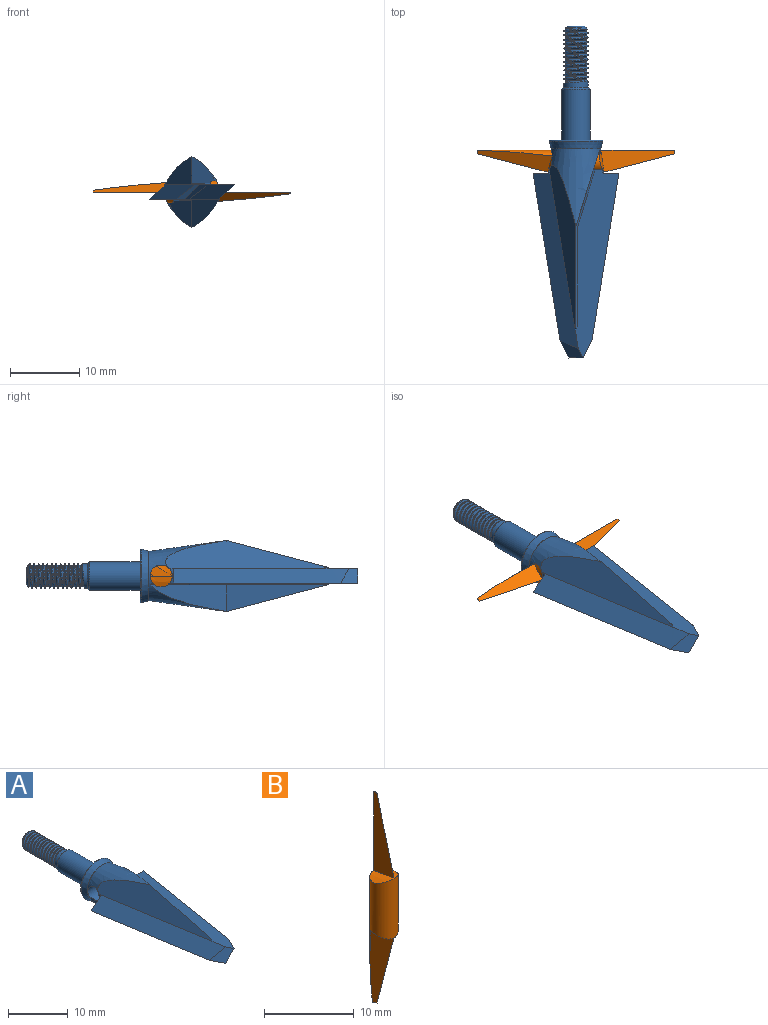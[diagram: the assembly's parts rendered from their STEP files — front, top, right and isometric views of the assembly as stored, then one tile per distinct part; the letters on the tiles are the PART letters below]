
ASSEMBLY  parts=2 mates=1
PART A: 56 faces, bbox 12.4x48x10.3 mm
  f0: plane 23.64x4.12mm, normal (0.85,-0.14,-0.52), area 71mm2, adj f1,f4,f5,f27,f29,f53,f55
  f1: plane 14.73x0.25mm, normal (-0.71,0,-0.71), area 5.2mm2, adj f0,f10,f29,f51,f55
  f2: plane 23.86x4.12mm, normal (-0.85,-0.14,0.52), area 71mm2, adj f3,f5,f9,f23,f28,f53,f54
  f3: plane 14.73x0.25mm, normal (0.71,0,0.71), area 5.2mm2, adj f2,f8,f12,f23,f54
  f4: plane 0.56x0.18mm, normal (0,0,-1), area 0.1mm2, adj f0,f7,f16,f53
  f5: cone r=3.56mm half-angle=8deg, axis (0,-1,0), area 89.4mm2, adj f0,f2,f11,f19,f23,f24,f29,f30
  f6: cone r=3.56mm half-angle=8deg, axis (0,-1,0), area 0.6mm2, adj f9,f10,f18,f31,f53
  f7: cone r=3.56mm half-angle=8deg, axis (0,-1,0), area 0.6mm2, adj f4,f8,f16,f17,f53
  f8: plane 27.23x6.33mm, normal (0,0,1), area 91.9mm2, adj f3,f7,f12,f17,f25,f26,f27,f28
  f9: plane 0.56x0.18mm, normal (0,0,1), area 0.1mm2, adj f2,f6,f31,f53
  f10: plane 27.23x6.33mm, normal (0,0,-1), area 91.9mm2, adj f1,f6,f18,f25,f26,f27,f28,f51
  f11: plane 0.65x0.35mm, normal (-0.68,-0.21,-0.71), area 0.1mm2, adj f5,f30,f53
  f12: plane 8.48x2.76mm, normal (0.68,-0.21,0.71), area 3.1mm2, adj f3,f8,f24,f53
  f13: cylinder r=2.08mm len=7.37mm, axis (0,-1,0), area 96.4mm2, adj f15,f21
  f14: plane 3.66x3.66mm, normal (0,1,0), area 0.9mm2, adj f15,f32
  f15: cone r=1.83mm half-angle=45deg, axis (0,-1,0), area 4.4mm2, adj f13,f14
  f16: plane 0.22x0.18mm, normal (0,-1,0), area 0mm2, adj f4,f7,f27
  f17: plane 2.28x1.85mm, normal (0,1,0), area 2mm2, adj f7,f8,f27
  f18: plane 2.28x1.85mm, normal (0,1,0), area 2mm2, adj f6,f10,f28
  f19: plane 7.15x7.15mm, normal (0,-1,0), area 0.4mm2, adj f5,f20
  f20: cone r=3.94mm half-angle=16deg, axis (0,1,0), area 27mm2, adj f19,f22
  f21: plane 7.54x7.54mm, normal (0,1,0), area 31mm2, adj f13,f22
  f22: torus R=3.77mm, axis (0,1,0), area 5.7mm2, adj f20,f21
  f23: plane 14.69x3.87mm, normal (1,0,0), area 28.6mm2, adj f2,f3,f5,f24
  f24: plane 10.99x3.86mm, normal (0.96,-0.29,0), area 28.5mm2, adj f5,f12,f23,f52,f53
  f25: plane 3.33x2.51mm, normal (-0.66,-0.34,0.66), area 5.9mm2, adj f8,f10,f26,f28
  f26: plane 3.33x2.51mm, normal (0.66,-0.34,-0.66), area 5.9mm2, adj f8,f10,f25,f27
  f27: plane 25.35x6.54mm, normal (0.63,-0.1,-0.77), area 79.3mm2, adj f0,f8,f10,f16,f17,f26
  f28: plane 25.35x6.54mm, normal (-0.63,-0.1,0.77), area 79.3mm2, adj f2,f8,f10,f18,f25,f31
  f29: plane 14.69x3.87mm, normal (-1,0,0), area 28.6mm2, adj f0,f1,f5,f30
  f30: plane 10.99x3.86mm, normal (-0.96,-0.29,0), area 28.5mm2, adj f5,f11,f29,f51,f53
  f31: plane 0.22x0.18mm, normal (0,-1,0), area 0mm2, adj f6,f9,f28
  f32: cylinder r=1.75mm len=3.51mm, axis (0,-1,0), area 7.4mm2, adj f14,f33,f47,f48,f50
  f33: cylinder r=1.75mm len=3.51mm, axis (0,-1,0), area 1mm2, adj f32,f34,f48,f50
  f34: cylinder r=1.75mm len=3.51mm, axis (0,-1,0), area 1mm2, adj f33,f35,f48,f50
  f35: cylinder r=1.75mm len=3.51mm, axis (0,-1,0), area 1mm2, adj f34,f36,f48,f50
  f36: cylinder r=1.75mm len=3.51mm, axis (0,-1,0), area 1mm2, adj f35,f37,f48,f50
  f37: cylinder r=1.75mm len=3.51mm, axis (0,-1,0), area 1mm2, adj f36,f38,f48,f50
  f38: cylinder r=1.75mm len=3.51mm, axis (0,-1,0), area 1mm2, adj f37,f39,f48,f50
  f39: cylinder r=1.75mm len=3.51mm, axis (0,-1,0), area 1mm2, adj f38,f40,f48,f50
  f40: cylinder r=1.75mm len=3.51mm, axis (0,-1,0), area 1mm2, adj f39,f41,f48,f50
  f41: cylinder r=1.75mm len=3.51mm, axis (0,-1,0), area 1mm2, adj f40,f42,f48,f50
  f42: cylinder r=1.75mm len=3.51mm, axis (0,-1,0), area 1mm2, adj f41,f43,f48,f50
  f43: cylinder r=1.75mm len=3.51mm, axis (0,-1,0), area 1mm2, adj f42,f44,f48,f50
  f44: cylinder r=1.75mm len=1.33mm, axis (0,-1,0), area 0.1mm2, adj f43,f46,f50
  f45: plane 2.49x2.49mm, normal (0,1,0), area 4.9mm2, adj f46
  f46: cone r=1.24mm half-angle=45deg, axis (0,-1,0), area 4.6mm2, adj f44,f45,f48,f49,f50
  f47: plane 0.55x0.27mm, normal (0,0,-1), area 0.1mm2, adj f32,f48,f49,f50
  f48: bspline ~8.47x4.05mm, area 45.1mm2, adj f32,f33,f34,f35,f36,f37,f38,f39
  f49: cylinder r=1.48mm len=8.16mm, axis (0,1,0), area 20.7mm2, adj f46,f47,f48,f50
  f50: bspline ~8.23x4.05mm, area 41.3mm2, adj f32,f33,f34,f35,f36,f37,f38,f39
  f51: plane 8.48x2.76mm, normal (-0.68,-0.21,-0.71), area 3.1mm2, adj f1,f10,f30,f53
  f52: plane 0.65x0.35mm, normal (0.68,-0.21,0.71), area 0.1mm2, adj f5,f24,f53
  f53: cylinder r=1.59mm len=8.06mm, axis (-1,0,0), area 68.9mm2, adj f0,f2,f4,f5,f6,f7,f8,f9
  f54: plane 0.38x0.38mm, normal (0.71,-0.71,0), area 0.1mm2, adj f2,f3,f8
  f55: plane 0.38x0.38mm, normal (-0.71,-0.71,0), area 0.1mm2, adj f0,f1,f10
PART B: 11 faces, bbox 3.4x3.2x28.6 mm
  f0: cylinder r=1.59mm len=28.58mm, axis (0,0,-1), area 93.6mm2, adj f1,f2,f3,f4,f5,f6,f7,f8
  f1: plane 0.51x0.27mm, normal (0,0,-1), area 0.1mm2, adj f0,f3,f9
  f2: plane 0.51x0.27mm, normal (0,0,1), area 0.1mm2, adj f0,f4,f7
  f3: plane 10.69x3.18mm, normal (1,0,0), area 19.6mm2, adj f0,f1,f6,f9
  f4: plane 10.69x3.18mm, normal (-1,0,0), area 19.6mm2, adj f0,f2,f5,f7
  f5: cone r=3.56mm half-angle=8deg, axis (0,-1,0), area 4.1mm2, adj f0,f4
  f6: cone r=3.56mm half-angle=8deg, axis (0,-1,0), area 4.1mm2, adj f0,f3
  f7: plane 10.85x3.15mm, normal (0.87,-0.48,0.13), area 18.9mm2, adj f0,f2,f4,f8
  f8: cone r=3.56mm half-angle=8deg, axis (0,-1,0), area 1.6mm2, adj f0,f7
  f9: plane 10.85x3.15mm, normal (-0.87,-0.48,-0.13), area 18.9mm2, adj f0,f1,f3,f10
  f10: cone r=3.56mm half-angle=8deg, axis (0,-1,0), area 1.6mm2, adj f0,f9
PLACE A at identity fixed
PLACE B rot(axis=(0,1,0),90deg) t=(0,3.63,0)mm
MATE cylindrical A.f53 <-> B.f0  axis (-1,0,0) through (0,1.78,0)mm
